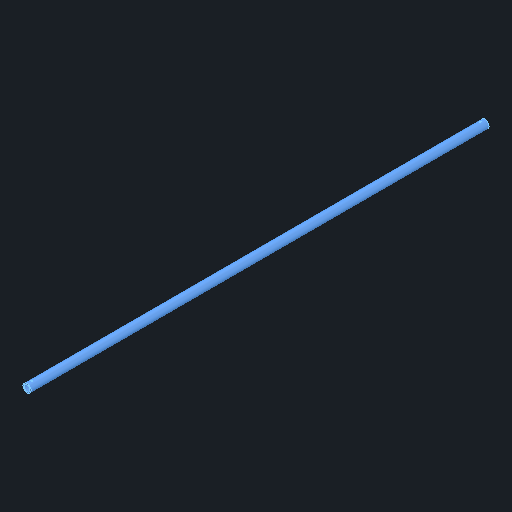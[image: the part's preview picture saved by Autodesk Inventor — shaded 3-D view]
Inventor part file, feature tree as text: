
AUTODESK INVENTOR PART (.ipt)
format: ipt  version: 2024 (Build 280153000, 153)  size: 99,840 bytes
history: native  units: in
note: dims shown in document units (in); Inventor stores cm internally (conversion verified against a paired STEP export)
features: mirror x1
ambient origin geometry x8: Origin, YZ Plane, XZ Plane, XY Plane, X Axis, Y Axis, Z Axis, Center Point
bodies: Solid1 (feature_tree)
feature tree (1):
  mirror  "Mirror1"
